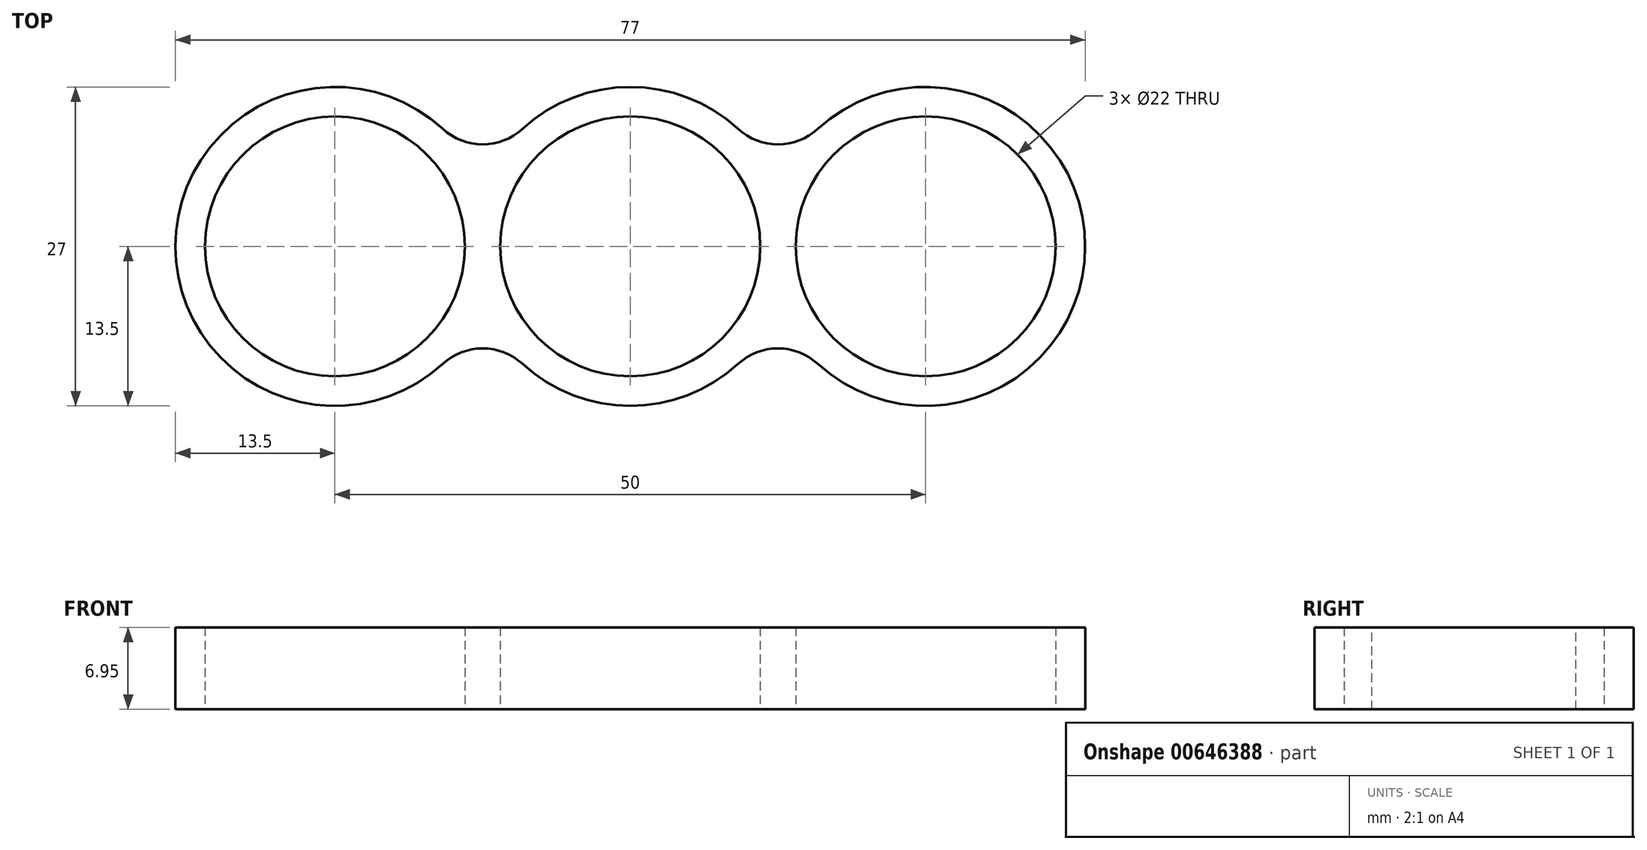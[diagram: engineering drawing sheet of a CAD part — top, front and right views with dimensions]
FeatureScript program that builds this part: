
annotation { "Feature Type Name" : "Feature", "Feature Type Description" : "" }
export const myFeature = defineFeature(function(context is Context, id is Id, definition is map)
    precondition{}
    {
        {
            var Q0;
            Q0=qCreatedBy(makeId("Top.planeOp"),FACE);
            var sketch = newSketch(context, id + "F0", { "sketchPlane" : qUnion([Q0])});
            skCircle(sketch, "E0", {"center": v(0, 0) * mm, "radius": 11 * mm});
            skArc(sketch, "E1", {"start": v(12.5, 5.1) * mm, "mid": v(0, 13.5) * mm, "end": v(-12.5, 5.1) * mm});
            skCircle(sketch, "E2", {"center": v(25, 0) * mm, "radius": 11 * mm});
            skArc(sketch, "E3", {"start": v(12.5, -5.1) * mm, "mid": v(38.5, 0) * mm, "end": v(12.5, 5.1) * mm});
            skArc(sketch, "E4.MirrorC", {"start": v(-12.5, -5.1) * mm, "mid": v(-38.5, 0) * mm, "end": v(-12.5, 5.1) * mm});
            skCircle(sketch, "E5.MirrorC", {"center": v(-25, 0) * mm, "radius": 11 * mm});
            skArc(sketch, "E6.trimOffspring", {"start": v(-12.5, -5.1) * mm, "mid": v(0, -13.5) * mm, "end": v(12.5, -5.1) * mm});
            skSolve(sketch);
        }
        {
            var Q0;
            Q0=makeQuery(id+"F0.imprint","IMPRINT",FACE,{"disambiguationData":[TD([[makeQuery(id+"F0.imprint","IMPRINT",EDGE,{"derivedFrom":sQuery(id+"F0.wireOp",EDGE,"E0")}),-1.0]])]});
            extrude(context, id + "F1", {"entities" : qUnion([Q0]), "depth" : 6.95 * mm, "offsetDistance" : 25 * mm});
        }
        {
            var Q0;
            Q0=makeQuery(id+"F1.opExtrude","SWEPT_EDGE",EDGE,{"disambiguationData":[OSD([sQuery(id+"F0.wireOp",EDGE,"E4.MirrorC"),sQuery(id+"F0.wireOp",EDGE,"E6.trimOffspring")])]});
            var Q1;
            Q1=makeQuery(id+"F1.opExtrude","SWEPT_EDGE",EDGE,{"disambiguationData":[OSD([sQuery(id+"F0.wireOp",EDGE,"E3"),sQuery(id+"F0.wireOp",EDGE,"E6.trimOffspring")])]});
            var Q2;
            Q2=makeQuery(id+"F1.opExtrude","SWEPT_EDGE",EDGE,{"disambiguationData":[OSD([sQuery(id+"F0.wireOp",EDGE,"E1"),sQuery(id+"F0.wireOp",EDGE,"E3")])]});
            var Q3;
            Q3=makeQuery(id+"F1.opExtrude","SWEPT_EDGE",EDGE,{"disambiguationData":[OSD([sQuery(id+"F0.wireOp",EDGE,"E1"),sQuery(id+"F0.wireOp",EDGE,"E4.MirrorC")])]});
            fillet(context, id + "F2", {"entities" : qUnion([Q0, Q1, Q2, Q3]), "radius" : 5 * mm, "tangentPropagation" : true, "allowEdgeOverflow" : false});
        }
    });
